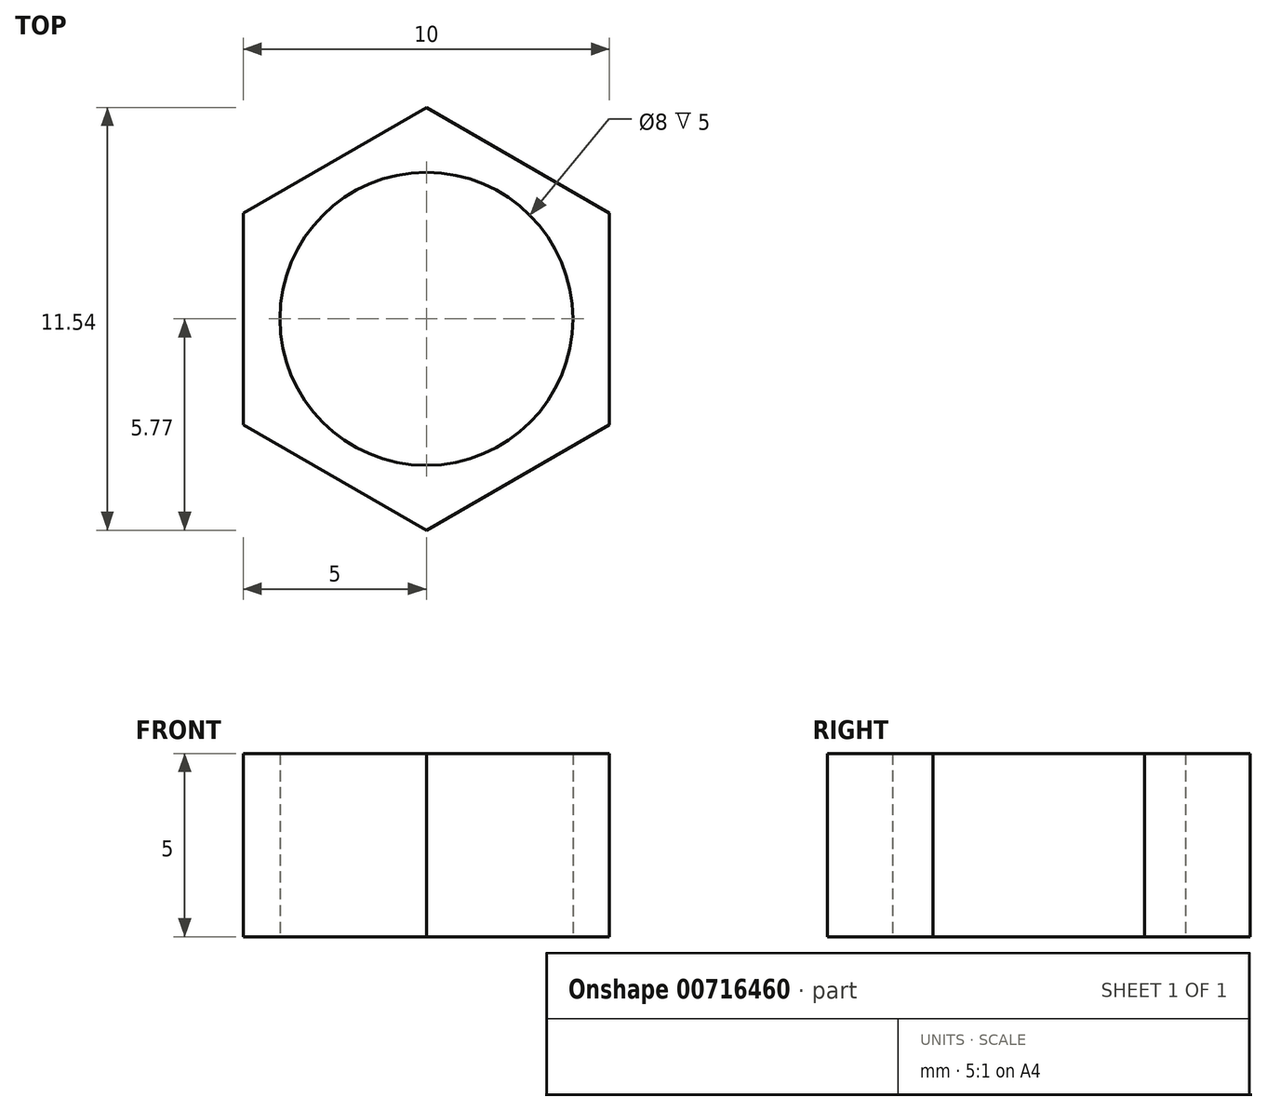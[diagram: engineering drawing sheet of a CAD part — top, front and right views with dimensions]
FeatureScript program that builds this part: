
annotation { "Feature Type Name" : "Feature", "Feature Type Description" : "" }
export const myFeature = defineFeature(function(context is Context, id is Id, definition is map)
    precondition{}
    {
        {
            var Q0;
            Q0=qCreatedBy(makeId("Top.planeOp"),FACE);
            var sketch = newSketch(context, id + "F0", { "sketchPlane" : qUnion([Q0])});
            skCircle(sketch, "E0", {"center": v(0, 0) * mm, "radius": 5 * mm});
            skLineSegment(sketch, "E1.0", {"start": v(5, 2.89) * mm, "end": v(5, -2.89) * mm});
            skLineSegment(sketch, "E1.1", {"start": v(5, -2.89) * mm, "end": v(0, -5.77) * mm});
            skLineSegment(sketch, "E1.2", {"start": v(0, -5.77) * mm, "end": v(-5, -2.89) * mm});
            skLineSegment(sketch, "E1.3", {"start": v(-5, -2.89) * mm, "end": v(-5, 2.89) * mm});
            skLineSegment(sketch, "E1.4", {"start": v(-5, 2.89) * mm, "end": v(0, 5.77) * mm});
            skLineSegment(sketch, "E1.5", {"start": v(0, 5.77) * mm, "end": v(5, 2.89) * mm});
            skPoint(sketch, "E1.0.midPoint", {"position": v(5, 0) * mm});
            skCircle(sketch, "E2", {"center": v(0, 0) * mm, "radius": 4 * mm});
            skSolve(sketch);
        }
        {
            var Q0;
            Q0 = qSketchRegion(id + "F0", true);
            extrude(context, id + "F1", {"entities" : qUnion([Q0]), "depth" : 5 * mm, "offsetDistance" : 25 * mm});
        }
    });
